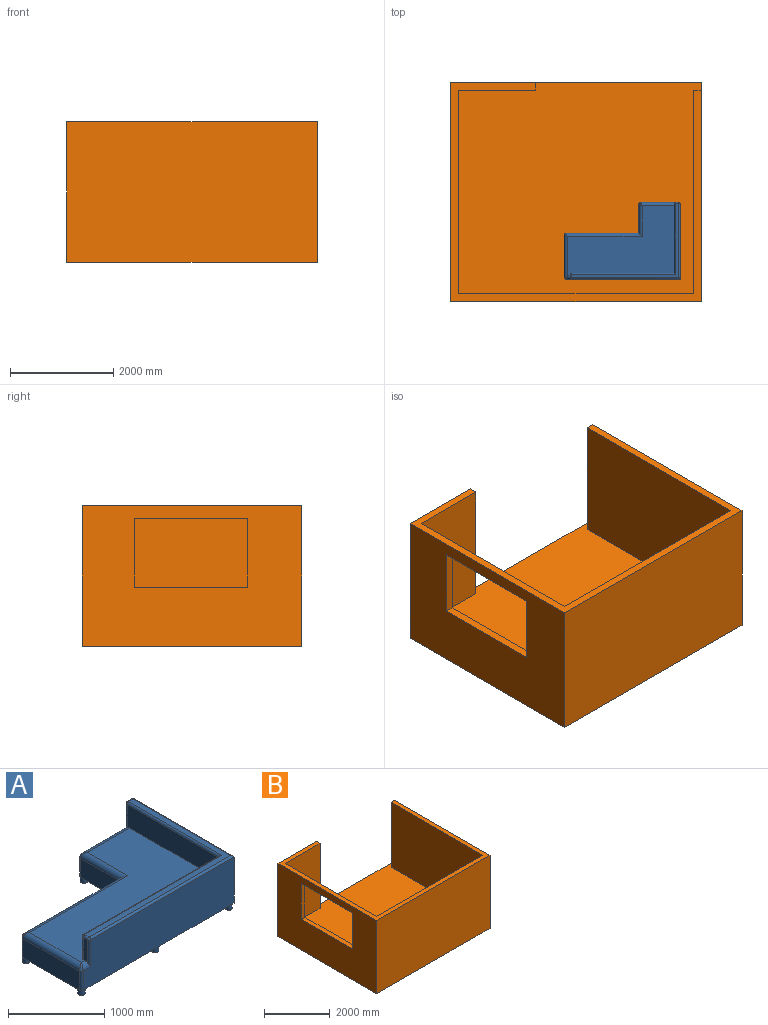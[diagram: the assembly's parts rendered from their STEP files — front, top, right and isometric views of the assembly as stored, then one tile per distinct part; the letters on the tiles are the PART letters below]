
ASSEMBLY  parts=2 mates=1
PART A: 56 faces, bbox 2247.9x1485.9x673.1 mm
  f0: plane 1422.4x241.3mm, normal (0,1,0), area 343225.1mm2, adj f6,f8,f14,f46,f51
  f1: plane 838.2x241.3mm, normal (-1,0,0), area 202257.7mm2, adj f6,f8,f13,f46,f47,f53
  f2: plane 2222.5x584.2mm, normal (0,-1,0), area 1259191mm2, adj f7,f8,f9,f13,f42,f44,f47,f55
  f3: plane 2082.8x1435.1mm, normal (0,0,1), area 219354.4mm2, adj f33,f34,f37,f40,f41,f42
  f4: plane 38.1x38.1mm, normal (0,0,-1), area 173.1mm2, adj f10,f14,f24,f45
  f5: plane 38.1x38.1mm, normal (0,0,-1), area 173.1mm2, adj f9,f10,f22,f35
  f6: plane 38.1x38.1mm, normal (0,0,-1), area 173.1mm2, adj f0,f1,f20,f46
  f7: plane 38.1x38.1mm, normal (0,0,-1), area 311.5mm2, adj f2,f9,f18
  f8: plane 2247.9x1485.9mm, normal (0,0,-1), area 2442482.6mm2, adj f0,f1,f2,f9,f10,f14,f16,f18
  f9: plane 1460.5x584.2mm, normal (1,0,0), area 853224.1mm2, adj f2,f5,f7,f8,f35,f40
  f10: plane 749.3x584.2mm, normal (0,1,0), area 202580.2mm2, adj f4,f5,f8,f31,f34,f35,f45,f48
  f11: plane 1346.2x292.1mm, normal (-1,0,0), area 376282.5mm2, adj f12,f15,f31,f33,f48
  f12: plane 1993.9x279.4mm, normal (0,1,0), area 557095.7mm2, adj f11,f15,f36,f37
  f13: plane 38.1x38.1mm, normal (0,0,-1), area 173.1mm2, adj f1,f2,f16,f47
  f14: plane 571.5x241.3mm, normal (-1,0,0), area 137902.9mm2, adj f0,f4,f8,f45,f50
  f15: plane 2070.1x1358.9mm, normal (0,0,1), area 1846425.1mm2, adj f11,f12,f30,f36,f48,f50,f51,f53
  f16: cylinder r=38.1mm len=76.2mm, axis (0,0,1), area 15201.2mm2, adj f8,f13,f17
  f17: plane 76.2x76.2mm, normal (0,0,-1), area 4560.4mm2, adj f16
  f18: cylinder r=38.1mm len=76.2mm, axis (0,0,1), area 15201.2mm2, adj f7,f8,f19
  f19: plane 76.2x76.2mm, normal (0,0,-1), area 4560.4mm2, adj f18
  f20: cylinder r=38.1mm len=76.2mm, axis (0,0,1), area 15201.2mm2, adj f6,f8,f21
  f21: plane 76.2x76.2mm, normal (0,0,-1), area 4560.4mm2, adj f20
  f22: cylinder r=38.1mm len=76.2mm, axis (0,0,1), area 15201.2mm2, adj f5,f8,f23
  f23: plane 76.2x76.2mm, normal (0,0,-1), area 4560.4mm2, adj f22
  f24: cylinder r=38.1mm len=76.2mm, axis (0,0,1), area 15201.2mm2, adj f4,f8,f25
  f25: plane 76.2x76.2mm, normal (0,0,-1), area 4560.4mm2, adj f24
  f26: cylinder r=38.1mm len=76.2mm, axis (0,0,1), area 15201.2mm2, adj f8,f27
  f27: plane 76.2x76.2mm, normal (0,0,-1), area 4560.4mm2, adj f26
  f28: cylinder r=38.1mm len=76.2mm, axis (0,0,1), area 15201.2mm2, adj f8,f29
  f29: plane 76.2x76.2mm, normal (0,0,-1), area 4560.4mm2, adj f28
  f30: plane 292.1x63.5mm, normal (-1,0,0), area 17896.1mm2, adj f15,f36,f41,f44,f55
  f31: cylinder r=25.4mm len=342.9mm, axis (0,0,1), area 12551.5mm2, adj f10,f11,f32,f48
  f32: sphere r=25.4mm, area 1013.4mm2, adj f31,f33,f34
  f33: cylinder r=25.4mm len=1371.6mm, axis (0,1,0), area 54079.2mm2, adj f3,f11,f32,f37
  f34: cylinder r=25.4mm len=63.5mm, axis (1,0,0), area 2533.5mm2, adj f3,f10,f32,f38
  f35: cylinder r=25.4mm len=584.2mm, axis (0,0,-1), area 23308.5mm2, adj f5,f9,f10,f38
  f36: cylinder r=25.4mm len=279.4mm, axis (0,0,-1), area 11147.6mm2, adj f12,f15,f30,f39
  f37: cylinder r=25.4mm len=2019.3mm, axis (1,0,0), area 79921.3mm2, adj f3,f12,f33,f39
  f38: sphere r=25.4mm, area 1013.4mm2, adj f34,f35,f40
  f39: sphere r=25.4mm, area 1013.4mm2, adj f36,f37,f41
  f40: cylinder r=25.4mm len=1460.5mm, axis (0,-1,0), area 57903.1mm2, adj f3,f9,f38,f42
  f41: cylinder r=25.4mm len=63.5mm, axis (0,-1,0), area 2533.5mm2, adj f3,f30,f39,f43
  f42: cylinder r=25.4mm len=2108.2mm, axis (-1,0,0), area 83745.2mm2, adj f2,f3,f40,f43
  f43: sphere r=25.4mm, area 1013.4mm2, adj f41,f42,f44
  f44: cylinder r=25.4mm len=342.9mm, axis (0,0,1), area 12551.5mm2, adj f2,f30,f43,f55
  f45: cylinder r=25.4mm len=241.3mm, axis (0,0,-1), area 9627.4mm2, adj f4,f10,f14,f49
  f46: cylinder r=25.4mm len=241.3mm, axis (0,0,1), area 9627.4mm2, adj f0,f1,f6,f52
  f47: cylinder r=25.4mm len=241.3mm, axis (0,0,-1), area 9627.4mm2, adj f1,f2,f13,f54
  f48: cylinder r=63.5mm len=685.8mm, axis (-1,0,0), area 65061.3mm2, adj f10,f11,f15,f31,f49
  f49: bspline ~66.41x63.5mm, area 2687.2mm2, adj f45,f48,f50
  f50: cylinder r=63.5mm len=635mm, axis (0,-1,0), area 57925.2mm2, adj f14,f15,f49,f51
  f51: cylinder r=63.5mm len=1485.9mm, axis (1,0,0), area 142798.7mm2, adj f0,f15,f50,f52
  f52: bspline ~66.41x63.5mm, area 2687.2mm2, adj f46,f51,f53
  f53: cylinder r=63.5mm len=838.2mm, axis (0,-1,0), area 80844.8mm2, adj f1,f15,f52,f54
  f54: bspline ~66.41x63.5mm, area 2687.2mm2, adj f47,f53,f55
  f55: cylinder r=63.5mm len=114.3mm, axis (1,0,0), area 8056.7mm2, adj f2,f15,f30,f44,f54
PART B: 17 faces, bbox 4851.4x4241.8x2717.8 mm
  f0: plane 4241.8x2717.8mm, normal (-1,0,0), area 8598531.2mm2, adj f4,f5,f10,f12,f13,f14,f15,f16
  f1: plane 3937x2413mm, normal (1,0,0), area 6570148.2mm2, adj f2,f9,f10,f11,f13,f14,f15,f16
  f2: plane 2413x1498.6mm, normal (0,-1,0), area 3616121.8mm2, adj f1,f3,f10,f11
  f3: plane 2413x152.4mm, normal (1,0,0), area 367741.2mm2, adj f2,f4,f10,f11
  f4: plane 4851.4x2717.8mm, normal (0,1,0), area 5462569.7mm2, adj f0,f3,f6,f10,f11,f12
  f5: plane 4851.4x2717.8mm, normal (0,-1,0), area 13185134.9mm2, adj f0,f6,f10,f12
  f6: plane 4241.8x2717.8mm, normal (1,0,0), area 11160622.8mm2, adj f4,f5,f7,f10,f11,f12
  f7: plane 2413x152.4mm, normal (0,1,0), area 367741.2mm2, adj f6,f8,f10,f11
  f8: plane 3937x2413mm, normal (-1,0,0), area 9499981mm2, adj f7,f9,f10,f11
  f9: plane 4546.6x2413mm, normal (0,1,0), area 10970945.8mm2, adj f1,f8,f10,f11
  f10: plane 4851.4x4241.8mm, normal (0,0,1), area 2190963.4mm2, adj f0,f1,f2,f3,f4,f5,f6,f7
  f11: plane 4699x4089.4mm, normal (0,0,1), area 18387705.2mm2, adj f1,f2,f3,f4,f6,f7,f8,f9
  f12: plane 4851.4x4241.8mm, normal (0,0,-1), area 20578668.5mm2, adj f0,f4,f5,f6
  f13: plane 2197.1x152.4mm, normal (0,0,-1), area 334838mm2, adj f0,f1,f14,f16
  f14: plane 1333.5x152.4mm, normal (0,-1,0), area 203225.4mm2, adj f0,f1,f13,f15
  f15: plane 2197.1x152.4mm, normal (0,0,1), area 334838mm2, adj f0,f1,f14,f16
  f16: plane 1333.5x152.4mm, normal (0,1,0), area 203225.4mm2, adj f0,f1,f13,f15
PLACE A t=(951.68,-1684.83,63.5)mm
PLACE B at identity fixed
MATE planar A.f24 <-> B.f11  axis (0,0,-1) through (1256.48,-237.03,0)mm
